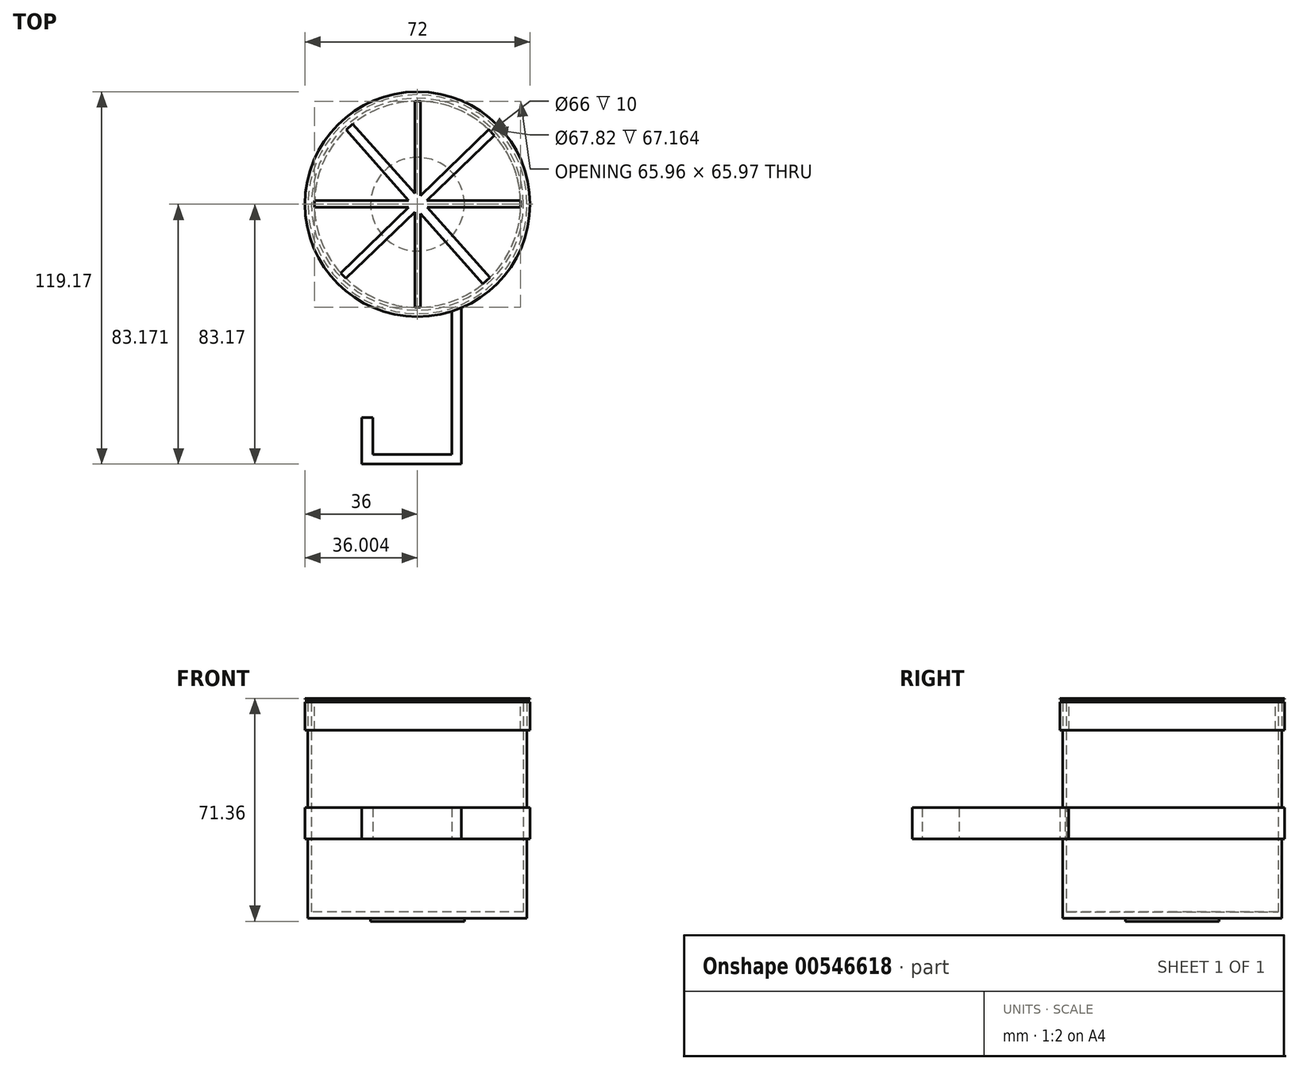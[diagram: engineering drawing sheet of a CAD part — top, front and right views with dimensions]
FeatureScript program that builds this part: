
annotation { "Feature Type Name" : "Feature", "Feature Type Description" : "" }
export const myFeature = defineFeature(function(context is Context, id is Id, definition is map)
    precondition{}
    {
        {
            var Q0;
            Q0=qCreatedBy(makeId("Top.planeOp"),FACE);
            var sketch = newSketch(context, id + "F0", { "sketchPlane" : qUnion([Q0])});
            skCircle(sketch, "E0", {"center": v(0, 0) * mm, "radius": 35.05 * mm});
            skCircle(sketch, "E1", {"center": v(0, 0) * mm, "radius": 33.9 * mm});
            skSolve(sketch);
        }
        {
            var Q0;
            Q0 = qSketchRegion(id + "F0", true);
            extrude(context, id + "F1", {"entities" : qUnion([Q0]), "depth" : 70.1 * mm, "offsetDistance" : 25.4 * mm});
        }
        {
            var Q0;
            Q0=qCreatedBy(makeId("Top.planeOp"),FACE);
            var sketch = newSketch(context, id + "F2", { "sketchPlane" : qUnion([Q0])});
            skCircle(sketch, "E2", {"center": v(0, 0) * mm, "radius": 35.05 * mm});
            skSolve(sketch);
        }
        {
            var Q0;
            Q0 = qSketchRegion(id + "F2", true);
            extrude(context, id + "F3", {"entities" : qUnion([Q0]), "operationType" : NewBodyOperationType.ADD, "depth" : 2 * mm, "offsetDistance" : 25.4 * mm});
        }
        {
            var Q0;
            Q0=makeQuery(id+"F0.imprint","IMPRINT",FACE,{"disambiguationData":[TD([[makeQuery(id+"F0.imprint","IMPRINT",EDGE,{"derivedFrom":sQuery(id+"F0.wireOp",EDGE,"E1")}),1.0]])]});
            var sketch = newSketch(context, id + "F4", { "sketchPlane" : qUnion([Q0])});
            skCircle(sketch, "E3", {"center": v(0, 0) * mm, "radius": 15 * mm});
            skSolve(sketch);
        }
        {
            var Q0;
            Q0 = qSketchRegion(id + "F4", true);
            extrude(context, id + "F5", {"entities" : qUnion([Q0]), "operationType" : NewBodyOperationType.ADD, "oppositeDirection" : true, "depth" : 1 * mm, "offsetDistance" : 25.4 * mm});
        }
        {
            var Q0;
            Q0=makeQuery(id+"F1.opExtrude","CAP_FACE",FACE,{"disambiguationData":[OSD([sQuery(id+"F0.wireOp",EDGE,"E0"),sQuery(id+"F0.wireOp",EDGE,"E1")])],"isStart":false});
            var sketch = newSketch(context, id + "F6", { "sketchPlane" : qUnion([Q0])});
            skCircle(sketch, "E4", {"center": v(0, 0) * mm, "radius": 36 * mm});
            skCircle(sketch, "E5", {"center": v(0, 0) * mm, "radius": 33 * mm});
            skSolve(sketch);
        }
        {
            var Q0;
            Q0 = qSketchRegion(id + "F6", true);
            extrude(context, id + "F7", {"entities" : qUnion([Q0]), "oppositeDirection" : true, "depth" : 10 * mm, "offsetDistance" : 25.4 * mm});
        }
        {
            var Q0;
            Q0=makeQuery(id+"F7.opExtrude","CAP_FACE",FACE,{"disambiguationData":[OSD([sQuery(id+"F6.wireOp",EDGE,"E4"),sQuery(id+"F6.wireOp",EDGE,"E5")])],"isStart":true});
            var sketch = newSketch(context, id + "F8", { "sketchPlane" : qUnion([Q0])});
            skCircle(sketch, "E6", {"center": v(0, 0) * mm, "radius": 36 * mm});
            skLineSegment(sketch, "E7.bottom", {"start": v(-0.86, 32.99) * mm, "end": v(0.96, 32.99) * mm});
            skLineSegment(sketch, "E7.top", {"start": v(-0.86, -32.99) * mm, "end": v(0.96, -32.99) * mm});
            skLineSegment(sketch, "E7.left", {"start": v(-0.86, 32.99) * mm, "end": v(-0.86, -32.99) * mm});
            skLineSegment(sketch, "E7.right", {"start": v(0.96, 32.99) * mm, "end": v(0.96, -32.99) * mm});
            skLineSegment(sketch, "E8.bottom", {"start": v(-32.98, 1.2) * mm, "end": v(32.99, 1.2) * mm});
            skLineSegment(sketch, "E8.top", {"start": v(-32.98, -0.98) * mm, "end": v(32.99, -0.98) * mm});
            skLineSegment(sketch, "E8.left", {"start": v(-32.98, 1.2) * mm, "end": v(-32.98, -0.98) * mm});
            skLineSegment(sketch, "E8.right", {"start": v(32.99, 1.2) * mm, "end": v(32.99, -0.98) * mm});
            skLineSegment(sketch, "E9", {"start": v(-23.05, 23.61) * mm, "end": v(-20.73, 25.68) * mm});
            skLineSegment(sketch, "E10", {"start": v(-20.73, 25.68) * mm, "end": v(23.23, -23.43) * mm});
            skLineSegment(sketch, "E11", {"start": v(23.23, -23.43) * mm, "end": v(20.9, -25.52) * mm});
            skLineSegment(sketch, "E12", {"start": v(20.9, -25.52) * mm, "end": v(-22.9, 23.86) * mm});
            skLineSegment(sketch, "E13", {"start": v(-24.54, -22.06) * mm, "end": v(-22.9, -23.76) * mm});
            skLineSegment(sketch, "E14", {"start": v(-22.9, -23.76) * mm, "end": v(24.54, 22.06) * mm});
            skLineSegment(sketch, "E15", {"start": v(24.54, 22.06) * mm, "end": v(22.8, 23.86) * mm});
            skLineSegment(sketch, "E16", {"start": v(22.8, 23.86) * mm, "end": v(-24.54, -22.06) * mm});
            skSolve(sketch);
        }
        {
            var Q0;
            Q0 = qSketchRegion(id + "F8", true);
            extrude(context, id + "F9", {"entities" : qUnion([Q0]), "operationType" : NewBodyOperationType.REMOVE, "oppositeDirection" : true, "depth" : 0.94 * mm, "offsetDistance" : 25.4 * mm});
        }
        {
            var Q0;
            Q0=qCreatedBy(makeId("Top.planeOp"),FACE);
            cPlane(context, id + "F10", {"entities" : qUnion([Q0]), "cplaneType" : CPlaneType.OFFSET, "offset" : 25.4 * mm, "width" : 152.4 * mm, "height" : 152.4 * mm});
        }
        {
            var Q0;
            Q0=qCreatedBy(id+"F10.planeOp",FACE);
            var sketch = newSketch(context, id + "F11", { "sketchPlane" : qUnion([Q0])});
            skCircle(sketch, "E17", {"center": v(0, 0) * mm, "radius": 35.05 * mm});
            skCircle(sketch, "E18", {"center": v(0, 0) * mm, "radius": 36 * mm});
            skLineSegment(sketch, "E19", {"start": v(14, -33.17) * mm, "end": v(14, -83.17) * mm});
            skLineSegment(sketch, "E20", {"start": v(14, -83.17) * mm, "end": v(-17.82, -83.17) * mm});
            skLineSegment(sketch, "E21", {"start": v(-17.82, -83.17) * mm, "end": v(-17.82, -68.24) * mm});
            skLineSegment(sketch, "E22", {"start": v(-17.82, -68.24) * mm, "end": v(-14.26, -68.24) * mm});
            skLineSegment(sketch, "E23", {"start": v(-14.26, -68.24) * mm, "end": v(-14.26, -80.05) * mm});
            skLineSegment(sketch, "E24", {"start": v(-14.26, -80.05) * mm, "end": v(10.93, -80.05) * mm});
            skLineSegment(sketch, "E25", {"start": v(10.93, -80.05) * mm, "end": v(10.93, -34.3) * mm});
            skLineSegment(sketch, "E26", {"start": v(10.93, -34.3) * mm, "end": v(14, -33.17) * mm});
            skSolve(sketch);
        }
        {
            var Q0;
            Q0 = qSketchRegion(id + "F11", true);
            extrude(context, id + "F12", {"entities" : qUnion([Q0]), "operationType" : NewBodyOperationType.ADD, "depth" : 10 * mm, "offsetDistance" : 25.4 * mm});
        }
        {
            var Q0;
            Q0 = qSketchRegion(id + "F11", true);
            extrude(context, id + "F13", {"entities" : qUnion([Q0]), "operationType" : NewBodyOperationType.ADD, "depth" : 10 * mm, "offsetDistance" : 25.4 * mm});
        }
        {
            var Q0;
            Q0 = qSketchRegion(id + "F8", true);
            extrude(context, id + "F14", {"entities" : qUnion([Q0]), "depth" : 0.25 * mm, "offsetDistance" : 25.4 * mm});
        }
    });
